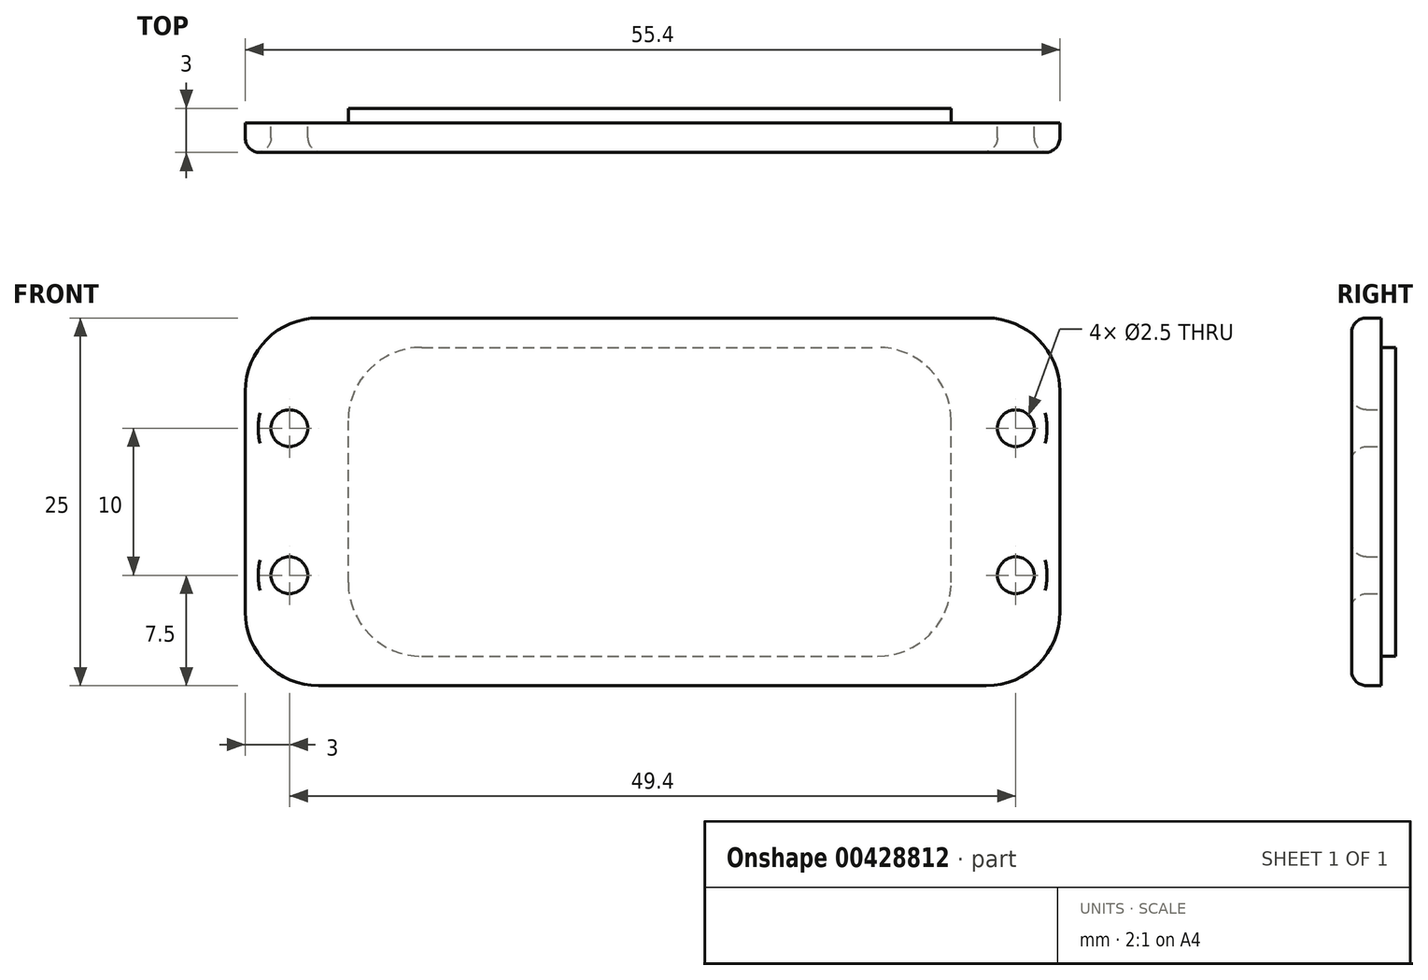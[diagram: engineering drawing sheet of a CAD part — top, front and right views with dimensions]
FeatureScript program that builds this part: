
annotation { "Feature Type Name" : "Feature", "Feature Type Description" : "" }
export const myFeature = defineFeature(function(context is Context, id is Id, definition is map)
    precondition{}
    {
        {
            var Q0;
            Q0=qCreatedBy(makeId("Front.planeOp"),FACE);
            var sketch = newSketch(context, id + "F0", { "sketchPlane" : qUnion([Q0])});
            skLineSegment(sketch, "E0.bottom", {"start": v(5, 0) * mm, "end": v(36, 0) * mm});
            skLineSegment(sketch, "E0.top", {"start": v(5, 21) * mm, "end": v(36, 21) * mm});
            skLineSegment(sketch, "E0.left", {"start": v(0, 5) * mm, "end": v(0, 16) * mm});
            skLineSegment(sketch, "E0.right", {"start": v(41, 5) * mm, "end": v(41, 16) * mm});
            skPoint(sketch, "E1.visualSharp", {"position": v(0, 21) * mm});
            skArc(sketch, "E1.filletArc", {"start": v(5, 21) * mm, "mid": v(1.46, 19.54) * mm, "end": v(0, 16) * mm});
            skPoint(sketch, "E2.visualSharp", {"position": v(41, 21) * mm});
            skArc(sketch, "E2.filletArc", {"start": v(41, 16) * mm, "mid": v(39.54, 19.54) * mm, "end": v(36, 21) * mm});
            skPoint(sketch, "E3.visualSharp", {"position": v(41, 0) * mm});
            skArc(sketch, "E3.filletArc", {"start": v(36, 0) * mm, "mid": v(39.54, 1.46) * mm, "end": v(41, 5) * mm});
            skPoint(sketch, "E4.visualSharp", {"position": v(0, 0) * mm});
            skArc(sketch, "E4.filletArc", {"start": v(0, 5) * mm, "mid": v(1.46, 1.46) * mm, "end": v(5, 0) * mm});
            skLineSegment(sketch, "E5.bottom", {"start": v(-4, 15.5) * mm, "end": v(45.4, 15.5) * mm});
            skLineSegment(sketch, "E5.top", {"start": v(-4, 5.5) * mm, "end": v(45.4, 5.5) * mm});
            skLineSegment(sketch, "E5.left", {"start": v(-4, 15.5) * mm, "end": v(-4, 5.5) * mm});
            skLineSegment(sketch, "E5.right", {"start": v(45.4, 15.5) * mm, "end": v(45.4, 5.5) * mm});
            skCircle(sketch, "E6", {"center": v(-4, 15.5) * mm, "radius": 1.25 * mm});
            skCircle(sketch, "E7", {"center": v(-4, 5.5) * mm, "radius": 1.25 * mm});
            skCircle(sketch, "E8", {"center": v(45.4, 15.5) * mm, "radius": 1.25 * mm});
            skCircle(sketch, "E9", {"center": v(45.4, 5.5) * mm, "radius": 1.25 * mm});
            skLineSegment(sketch, "E10.bottom", {"start": v(-2, 23) * mm, "end": v(43.4, 23) * mm});
            skLineSegment(sketch, "E10.top", {"start": v(-2, -2) * mm, "end": v(43.4, -2) * mm});
            skLineSegment(sketch, "E10.left", {"start": v(-7, 18) * mm, "end": v(-7, 3) * mm});
            skLineSegment(sketch, "E10.right", {"start": v(48.4, 18) * mm, "end": v(48.4, 3) * mm});
            skPoint(sketch, "E11.visualSharp", {"position": v(-7, 23) * mm});
            skArc(sketch, "E11.filletArc", {"start": v(-2, 23) * mm, "mid": v(-5.54, 21.54) * mm, "end": v(-7, 18) * mm});
            skPoint(sketch, "E12.visualSharp", {"position": v(-7, -2) * mm});
            skArc(sketch, "E12.filletArc", {"start": v(-7, 3) * mm, "mid": v(-5.54, -0.54) * mm, "end": v(-2, -2) * mm});
            skPoint(sketch, "E13.visualSharp", {"position": v(48.4, 23) * mm});
            skArc(sketch, "E13.filletArc", {"start": v(48.4, 18) * mm, "mid": v(46.94, 21.54) * mm, "end": v(43.4, 23) * mm});
            skPoint(sketch, "E14.visualSharp", {"position": v(48.4, -2) * mm});
            skArc(sketch, "E14.filletArc", {"start": v(43.4, -2) * mm, "mid": v(46.94, -0.54) * mm, "end": v(48.4, 3) * mm});
            skSolve(sketch);
        }
        {
            var Q0;
            Q0=makeQuery(id+"F0.imprint","IMPRINT",FACE,{"disambiguationData":[TD([[makeQuery(id+"F0.imprint","IMPRINT",EDGE,{"derivedFrom":sQuery(id+"F0.wireOp",EDGE,"E0.bottom")}),-1.0]])]});
            var Q1;
            Q1=makeQuery(id+"F0.imprint","IMPRINT",FACE,{"disambiguationData":[TD([[makeQuery(id+"F0.imprint","IMPRINT",EDGE,{"derivedFrom":sQuery(id+"F0.wireOp",EDGE,"E0.top")}),-1.0]])]});
            var Q2;
            {var subQ5=sQuery(id+"F0.wireOp",EDGE,"E5.top");var subQ6=sQuery(id+"F0.wireOp",EDGE,"E0.left");var subQ7=makeQuery(id+"F0.imprint","INTERSECT",VERTEX,{"derivedFrom":[subQ6,subQ5]});Q2=makeQuery(id+"F0.imprint","IMPRINT",FACE,{"disambiguationData":[TD([[makeQuery(id+"F0.imprint","IMPRINT",EDGE,{"disambiguationData":[TD([[subQ7,-1.0]])],"derivedFrom":subQ6}),1.0]])]});}
            var Q3;
            {var subQ0=sQuery(id+"F0.wireOp",EDGE,"E5.top");var subQ1=sQuery(id+"F0.wireOp",EDGE,"E0.left");var subQ2=makeQuery(id+"F0.imprint","INTERSECT",VERTEX,{"derivedFrom":[subQ1,subQ0]});Q3=makeQuery(id+"F0.imprint","IMPRINT",FACE,{"disambiguationData":[TD([[makeQuery(id+"F0.imprint","IMPRINT",EDGE,{"disambiguationData":[TD([[subQ2,-1.0]])],"derivedFrom":subQ1}),-1.0]])]});}
            var Q4;
            {var subQ0=sQuery(id+"F0.wireOp",EDGE,"E5.top");var subQ1=sQuery(id+"F0.wireOp",EDGE,"E0.right");var subQ2=makeQuery(id+"F0.imprint","INTERSECT",VERTEX,{"derivedFrom":[subQ1,subQ0]});Q4=makeQuery(id+"F0.imprint","IMPRINT",FACE,{"disambiguationData":[TD([[makeQuery(id+"F0.imprint","IMPRINT",EDGE,{"disambiguationData":[TD([[subQ2,-1.0]])],"derivedFrom":subQ1}),-1.0]])]});}
            var Q5;
            Q5=makeQuery(id+"F0.imprint","IMPRINT",FACE,{"disambiguationData":[TD([[makeQuery(id+"F0.imprint","IMPRINT",EDGE,{"derivedFrom":sQuery(id+"F0.wireOp",EDGE,"E0.bottom")}),1.0]])]});
            extrude(context, id + "F1", {"entities" : qUnion([Q0, Q1, Q2, Q3, Q4, Q5]), "depth" : 2 * mm});
        }
        {
            var Q0;
            Q0=makeQuery(id+"F0.imprint","IMPRINT",FACE,{"disambiguationData":[TD([[makeQuery(id+"F0.imprint","IMPRINT",EDGE,{"derivedFrom":sQuery(id+"F0.wireOp",EDGE,"E0.top")}),-1.0]])]});
            var Q1;
            {var subQ0=sQuery(id+"F0.wireOp",EDGE,"E5.top");var subQ1=sQuery(id+"F0.wireOp",EDGE,"E0.left");var subQ2=makeQuery(id+"F0.imprint","INTERSECT",VERTEX,{"derivedFrom":[subQ1,subQ0]});Q1=makeQuery(id+"F0.imprint","IMPRINT",FACE,{"disambiguationData":[TD([[makeQuery(id+"F0.imprint","IMPRINT",EDGE,{"disambiguationData":[TD([[subQ2,-1.0]])],"derivedFrom":subQ1}),-1.0]])]});}
            var Q2;
            Q2=makeQuery(id+"F0.imprint","IMPRINT",FACE,{"disambiguationData":[TD([[makeQuery(id+"F0.imprint","IMPRINT",EDGE,{"derivedFrom":sQuery(id+"F0.wireOp",EDGE,"E0.bottom")}),1.0]])]});
            extrude(context, id + "F2", {"entities" : qUnion([Q0, Q1, Q2]), "operationType" : NewBodyOperationType.ADD, "oppositeDirection" : true, "depth" : 1 * mm});
        }
        {
            var Q0;
            Q0=makeQuery(id+"F1.opExtrude","CAP_FACE",FACE,{"disambiguationData":[OSD([sQuery(id+"F0.wireOp",EDGE,"E6"),sQuery(id+"F0.wireOp",EDGE,"E7"),sQuery(id+"F0.wireOp",EDGE,"E8"),sQuery(id+"F0.wireOp",EDGE,"E9"),sQuery(id+"F0.wireOp",EDGE,"E10.bottom"),sQuery(id+"F0.wireOp",EDGE,"E10.top"),sQuery(id+"F0.wireOp",EDGE,"E10.left"),sQuery(id+"F0.wireOp",EDGE,"E10.right"),sQuery(id+"F0.wireOp",EDGE,"E11.filletArc"),sQuery(id+"F0.wireOp",EDGE,"E12.filletArc"),sQuery(id+"F0.wireOp",EDGE,"E13.filletArc"),sQuery(id+"F0.wireOp",EDGE,"E14.filletArc")])],"isStart":false});
            fillet(context, id + "F3", {"entities" : qUnion([Q0]), "radius" : 1 * mm, "tangentPropagation" : true, "allowEdgeOverflow" : false});
        }
    });
